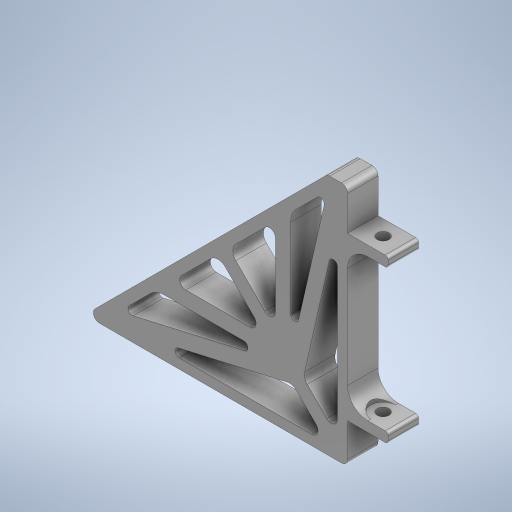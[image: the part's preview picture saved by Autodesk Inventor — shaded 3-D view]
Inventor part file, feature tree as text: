
AUTODESK INVENTOR PART (.ipt)
format: ipt  version: 2024.1 (Build 281209000, 209)  size: 581,632 bytes
history: native  units: mm
features: fillet x9, sketch x5, extrude x3, hole x2, projected_geometry x1
ambient origin geometry x8: Origin, YZ Plane, XZ Plane, XY Plane, X Axis, Y Axis, Z Axis, Center Point
bodies: Body1 (feature_tree)
feature tree (20):
  extrude  "Extrusion3"  Depth=4.0mm
  fillet  "Fillet2"  Radius=165.0mm
  sketch  "Sketch7"  dims[d43=45.0deg d44=15.0mm d45=0.0mm d46=3.0mm d57=5.0mm d61=7.5mm d63=7.5mm d66=3.75mm d67=7.5mm d70=5.0mm]
  extrude  "Extrusion6"  Depth=15.0mm TaperAngle=0.0deg
  fillet  "Fillet28"  Radius=3.0mm
  fillet  "Fillet29"  Radius=5.0mm
  fillet  "Fillet30"  Radius=7.5mm
  fillet  "Fillet31"  Radius=7.5mm
  fillet  "Fillet32"  Radius=3.75mm
  fillet  "Fillet33"  Radius=7.5mm
  fillet  "Fillet34"  Radius=5.0mm
  hole  "Hole7"  [1 undecoded]
  hole  "Hole8"  [1 undecoded]
  extrude  "Extrusion12"  Depth=5.0mm
  fillet  "Fillet35"  Radius=5.0mm
  sketch  "Sketch1"  dims[d3=30.0mm d41=4.0mm d42=165.0mm]
  sketch  "Sketch16"  dims[d71=0.0mm d72=0.0mm d75=3.75mm]
  sketch  "Sketch18"  dims[d173=20.0mm d174=20.0mm]
  sketch  "Sketch19"  dims[d175=80.0mm d176=5.0mm d177=5.0mm d178=2.0mm d179=10.0mm d180=5.0mm d181=3.0mm d182=5.0mm d183=3.0mm d184=10.0mm d185=5.8mm d186=6.0mm d187=10.0mm d188=5.0mm d189=90.0deg d190=8.0mm d191=20.594885mm d192=7.5mm d196=5.8mm d197=6.0mm d198=4.0mm d199=2.0mm d200=90.0deg d201=8.0mm d202=20.594885mm d203=7.5mm d204=12.0mm d205=10.0mm d206=0.0mm d207=1.5mm d117=0.0mm d118=0.0mm d119=0.0mm d120=0.0mm d125=0.5mm d126=0.872665mm d127=0.5mm d128=0.872665mm d129=0.0mm d130=0.0mm d131=0.0mm d132=0.0mm]
  projected_geometry  "Project Cut Edges1"
note: 2 required parameter values undecoded (feature->parameter linkage not recoverable at this tier; creation-order binding heuristic only, values carry confidence <= 0.55)
